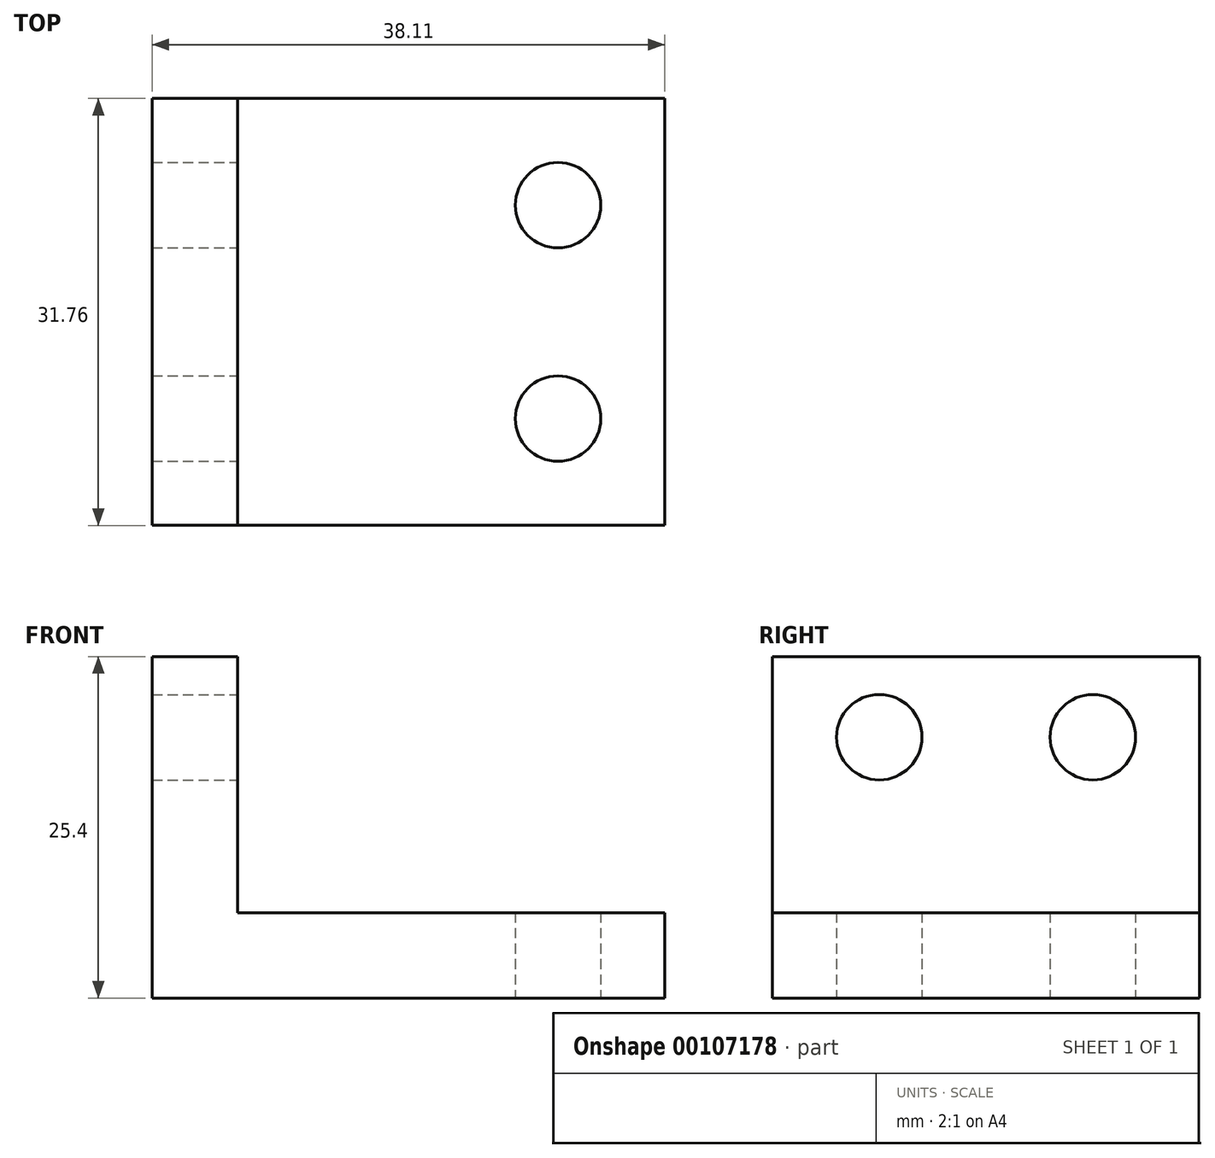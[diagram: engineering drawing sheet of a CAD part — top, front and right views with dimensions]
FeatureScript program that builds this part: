
annotation { "Feature Type Name" : "Feature", "Feature Type Description" : "" }
export const myFeature = defineFeature(function(context is Context, id is Id, definition is map)
    precondition{}
    {
        {
            var Q0;
            Q0=qCreatedBy(makeId("Top.planeOp"),FACE);
            var sketch = newSketch(context, id + "F0", { "sketchPlane" : qUnion([Q0])});
            skLineSegment(sketch, "E0.bottom", {"start": v(-15.88, 15.88) * mm, "end": v(15.88, 15.88) * mm});
            skLineSegment(sketch, "E0.top", {"start": v(-15.88, -15.87) * mm, "end": v(15.88, -15.87) * mm});
            skLineSegment(sketch, "E0.left", {"start": v(-15.88, 15.88) * mm, "end": v(-15.88, -15.87) * mm});
            skLineSegment(sketch, "E0.right", {"start": v(15.88, 15.87) * mm, "end": v(15.88, -15.88) * mm});
            skPoint(sketch, "E0.middle", {"position": v(0, 0) * mm});
            skLineSegment(sketch, "E1.bottom", {"start": v(-15.88, 15.87) * mm, "end": v(-22.23, 15.87) * mm});
            skLineSegment(sketch, "E1.top", {"start": v(-15.88, -15.87) * mm, "end": v(-22.22, -15.87) * mm});
            skLineSegment(sketch, "E1.left", {"start": v(-15.88, 15.87) * mm, "end": v(-15.87, -15.87) * mm});
            skLineSegment(sketch, "E1.right", {"start": v(-22.23, 15.88) * mm, "end": v(-22.22, -15.87) * mm});
            skCircle(sketch, "E2", {"center": v(7.94, 7.94) * mm, "radius": 3.18 * mm});
            skCircle(sketch, "E3", {"center": v(7.94, -7.94) * mm, "radius": 3.18 * mm});
            skSolve(sketch);
        }
        {
            var Q0;
            Q0=makeQuery(id+"F0.imprint","IMPRINT",FACE,{"disambiguationData":[TD([[makeQuery(id+"F0.imprint","IMPRINT",EDGE,{"derivedFrom":sQuery(id+"F0.wireOp",EDGE,"E0.bottom")}),-1.0]])]});
            extrude(context, id + "F1", {"entities" : qUnion([Q0]), "depth" : 6.35 * mm});
        }
        {
            var Q0;
            Q0=makeQuery(id+"F0.imprint","IMPRINT",FACE,{"disambiguationData":[TD([[makeQuery(id+"F0.imprint","IMPRINT",EDGE,{"derivedFrom":sQuery(id+"F0.wireOp",EDGE,"E1.bottom")}),1.0]])]});
            extrude(context, id + "F2", {"entities" : qUnion([Q0]), "operationType" : NewBodyOperationType.ADD, "depth" : 25.4 * mm});
        }
        {
            var Q0;
            Q0=makeQuery(id+"F2.opExtrude","SWEPT_FACE",FACE,{"disambiguationData":[OSD([sQuery(id+"F0.wireOp",EDGE,"E1.left")])]});
            var sketch = newSketch(context, id + "F3", { "sketchPlane" : qUnion([Q0])});
            skCircle(sketch, "E4", {"center": v(7.94, 19.4) * mm, "radius": 3.18 * mm});
            skCircle(sketch, "E5", {"center": v(-7.94, 19.4) * mm, "radius": 3.18 * mm});
            skSolve(sketch);
        }
        {
            var Q0;
            Q0=makeQuery(id+"F3.imprint","IMPRINT",FACE,{"disambiguationData":[TD([[makeQuery(id+"F3.imprint","IMPRINT",EDGE,{"derivedFrom":sQuery(id+"F3.wireOp",EDGE,"E5")}),1.0]])]});
            var Q1;
            Q1=makeQuery(id+"F3.imprint","IMPRINT",FACE,{"disambiguationData":[TD([[makeQuery(id+"F3.imprint","IMPRINT",EDGE,{"derivedFrom":sQuery(id+"F3.wireOp",EDGE,"E4")}),1.0]])]});
            extrude(context, id + "F4", {"entities" : qUnion([Q0, Q1]), "operationType" : NewBodyOperationType.REMOVE, "oppositeDirection" : true, "depth" : 25.4 * mm});
        }
    });
